# Revit family: Electronics_Commercial-Loudspeakers_Biamp_Compression-Driver-Horn_EN-H15
name_source: partatom
category: Communication Devices
units: mm (PartAtom-declared; Revit-internal decimal feet)

## family parameters
Cut with Voids When Loaded = No
Host = Face
Maintain Annotation Orientation = No
OmniClass Number = 23.85.10.11.14.14.14
OmniClass Title = Loudspeakers
Part Type = Normal
Room Calculation Point = No
Round Connector Dimension = Use Diameter
Shared = No

## types (1)
- EN-H15-G
    100V transformer power taps in watts = 15 - 7.5 - 3.75 - 1.87
    Bracket Material = Biamp - Metal - Gray
    Certificate ref = 1438/CPR/0355
    Closest RAL colour (subject to deviations) = RAL7035
    Colour = Grey
    Connector Description = Conductor; 15-7.5-3.75-1.87 W 100V
    Default Elevation = 48 "
    Depth = 11 "
    Description = EN-H15-G EN54-24 Certified Compression Driver Horn 15W
    Diameter = 8 "
    Frequency response in Hz = 400 - 12 k
    Housing Material = Biamp - Plastic - Gray
    IP rating = 66
    Loudspeaker system = Compression driver
    Low impedance dynamic power in watts = 15
    Main construction material = ABS plastic
    Manufacturer = Biamp
    Max SPL 1m in dB = 112.3
    Model = EN-H15-G
    Mounting system = 2 screws
    Operating temperatures = -50°C to +100°C
    Product Documentation Link = https://downloads.biamp.com
    Product Page URL = https://www.biamp.com
    Product data url = https://bimobject.com
    SPL 1W/1m in dB = 100.5
    URL = https://www.biamp.com
    Version = 1
    Vertical dispersion angle 1000 Hz = 180°
    Weight = 2.11 lb

## geometry (parser evidence)
native form markers: Sweep x4
no freeform markers — native parametric forms only
